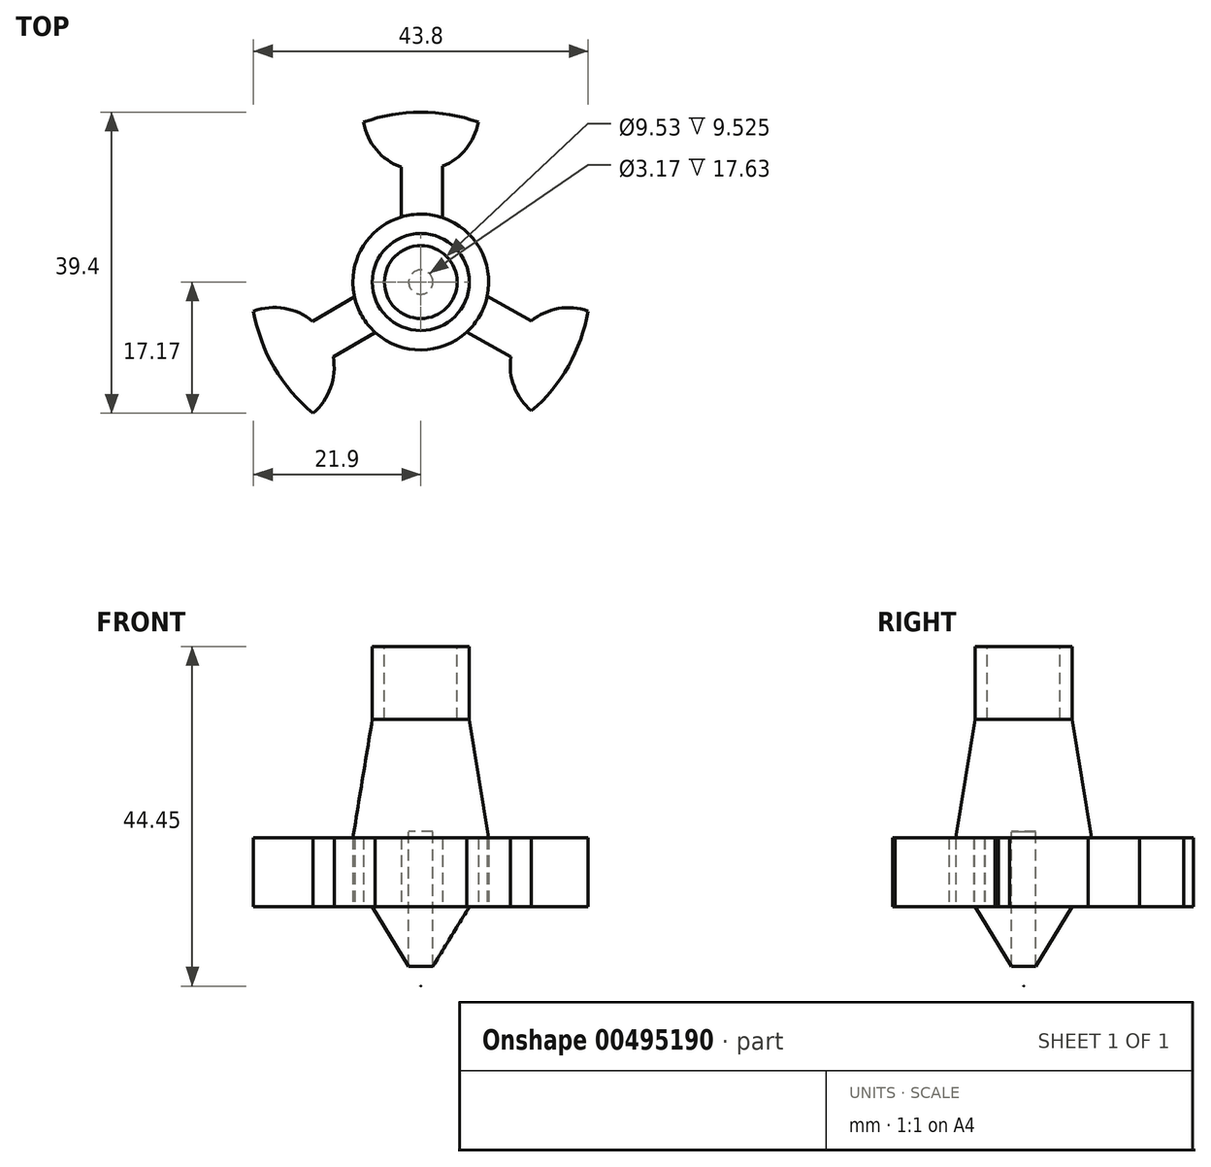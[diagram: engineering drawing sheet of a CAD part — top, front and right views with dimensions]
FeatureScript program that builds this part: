
annotation { "Feature Type Name" : "Feature", "Feature Type Description" : "" }
export const myFeature = defineFeature(function(context is Context, id is Id, definition is map)
    precondition{}
    {
        {
            var Q0;
            Q0=qCreatedBy(makeId("Front.planeOp"),FACE);
            var sketch = newSketch(context, id + "F0", { "sketchPlane" : qUnion([Q0])});
            skLineSegment(sketch, "E0", {"start": v(6.35, 34.05) * mm, "end": v(6.35, 24.53) * mm});
            skLineSegment(sketch, "E1", {"start": v(6.35, 0) * mm, "end": v(0, -10.4) * mm});
            skLineSegment(sketch, "E2.MirrorCS", {"start": v(-6.35, 0) * mm, "end": v(0, -10.4) * mm});
            skLineSegment(sketch, "E3.MirrorCS", {"start": v(-6.35, 34.05) * mm, "end": v(-6.35, 24.53) * mm});
            skLineSegment(sketch, "E4", {"start": v(6.35, 0) * mm, "end": v(22.23, 0) * mm});
            skLineSegment(sketch, "E5", {"start": v(22.23, 0) * mm, "end": v(22.23, 9.01) * mm});
            skLineSegment(sketch, "E6", {"start": v(22.23, 9.01) * mm, "end": v(8.89, 9.01) * mm});
            skLineSegment(sketch, "E7.MirrorCS", {"start": v(-22.23, 9.01) * mm, "end": v(-8.9, 9.01) * mm});
            skLineSegment(sketch, "E8.MirrorCS", {"start": v(-22.23, 0) * mm, "end": v(-22.23, 9.01) * mm});
            skLineSegment(sketch, "E9.MirrorCS", {"start": v(-6.35, 0) * mm, "end": v(-22.23, 0) * mm});
            skLineSegment(sketch, "E10", {"start": v(6.35, 24.53) * mm, "end": v(8.89, 9.01) * mm});
            skLineSegment(sketch, "E11", {"start": v(-6.35, 24.53) * mm, "end": v(-8.9, 9.01) * mm});
            skLineSegment(sketch, "E12", {"start": v(-6.35, 34.05) * mm, "end": v(6.35, 34.05) * mm});
            skLineSegment(sketch, "E13", {"start": v(0, -10.4) * mm, "end": v(0, 34.05) * mm});
            skSolve(sketch);
        }
        {
            var Q0;
            {var subQ0=sQuery(id+"F0.wireOp",EDGE,"E0");Q0=makeQuery(id+"F0.imprint","IMPRINT",FACE,{"disambiguationData":[TD([[makeQuery(id+"F0.imprint","IMPRINT",EDGE,{"derivedFrom":subQ0}),-1.0]])]});}
            var Q1;
            Q1=sQuery(id+"F0.wireOp",EDGE,"E13");
            revolve(context, id + "F1", {"entities" : qUnion([Q0]), "axis" : qUnion([Q1]), "revolveType" : RevolveType.FULL});
        }
        {
            var Q0;
            Q0=qCreatedBy(makeId("Top.planeOp"),FACE);
            var sketch = newSketch(context, id + "F2", { "sketchPlane" : qUnion([Q0])});
            skCircle(sketch, "E14", {"center": v(0, 0) * mm, "radius": 22.23 * mm});
            skArc(sketch, "E15", {"start": v(-7.5, 20.92) * mm, "mid": v(-5.82, 17.31) * mm, "end": v(-2.55, 15.05) * mm});
            skCircle(sketch, "E16", {"center": v(0, 0) * mm, "radius": 8.9 * mm});
            skPoint(sketch, "E17.orphan", {"position": v(0.8, -0.05) * mm});
            skArc(sketch, "E18.trimOffspring", {"start": v(2.83, 15.15) * mm, "mid": v(5.92, 17.42) * mm, "end": v(7.5, 20.92) * mm});
            skArc(sketch, "E19", {"start": v(-14.11, -17.17) * mm, "mid": v(-11.8, -13.83) * mm, "end": v(-11.47, -9.8) * mm});
            skArc(sketch, "E20", {"start": v(21.9, -3.8) * mm, "mid": v(18, -3.47) * mm, "end": v(14.46, -5.11) * mm});
            skLineSegment(sketch, "E21", {"start": v(-2.55, 15.05) * mm, "end": v(-2.55, 8.52) * mm});
            skLineSegment(sketch, "E22", {"start": v(2.83, 15.15) * mm, "end": v(2.83, 8.43) * mm});
            skLineSegment(sketch, "E23.trimOffspring", {"start": v(-11.47, -9.8) * mm, "end": v(-5.97, -6.59) * mm});
            skLineSegment(sketch, "E24.trimOffspring", {"start": v(-14.18, -5.14) * mm, "end": v(-8.68, -1.94) * mm});
            skLineSegment(sketch, "E25", {"start": v(11.8, -9.8) * mm, "end": v(6.04, -6.52) * mm});
            skLineSegment(sketch, "E26.MirrorCS", {"start": v(14.46, -5.11) * mm, "end": v(8.7, -1.84) * mm});
            skArc(sketch, "E27.trimOffspring", {"start": v(11.8, -9.8) * mm, "mid": v(12.2, -13.68) * mm, "end": v(14.49, -16.85) * mm});
            skArc(sketch, "E28.trimOffspring", {"start": v(-14.18, -5.14) * mm, "mid": v(-17.86, -3.44) * mm, "end": v(-21.9, -3.8) * mm});
            skSolve(sketch);
        }
        {
            var Q0;
            {var subQ0=sQuery(id+"F2.wireOp",EDGE,"E19");Q0=makeQuery(id+"F2.imprint","IMPRINT",FACE,{"disambiguationData":[TD([[makeQuery(id+"F2.imprint","IMPRINT",EDGE,{"derivedFrom":subQ0}),-1.0]])]});}
            var Q1;
            {var subQ0=sQuery(id+"F2.wireOp",EDGE,"E18.trimOffspring");Q1=makeQuery(id+"F2.imprint","IMPRINT",FACE,{"disambiguationData":[TD([[makeQuery(id+"F2.imprint","IMPRINT",EDGE,{"derivedFrom":subQ0}),-1.0]])]});}
            var Q2;
            {var subQ3=sQuery(id+"F2.wireOp",EDGE,"E15");Q2=makeQuery(id+"F2.imprint","IMPRINT",FACE,{"disambiguationData":[TD([[makeQuery(id+"F2.imprint","IMPRINT",EDGE,{"derivedFrom":subQ3}),-1.0]])]});}
            extrude(context, id + "F3", {"entities" : qUnion([Q0, Q1, Q2]), "operationType" : NewBodyOperationType.REMOVE, "depth" : 14.1 * mm});
        }
        {
            var Q0;
            Q0=makeQuery(id+"F1.opRevolve","SWEPT_FACE",FACE,{"disambiguationData":[OSD([sQuery(id+"F0.wireOp",EDGE,"E12")])]});
            var sketch = newSketch(context, id + "F4", { "sketchPlane" : qUnion([Q0])});
            skCircle(sketch, "E29", {"center": v(0, 0) * mm, "radius": 4.76 * mm});
            skSolve(sketch);
        }
        {
            var Q0;
            Q0=makeQuery(id+"F4.imprint","IMPRINT",FACE,{"disambiguationData":[TD([[makeQuery(id+"F4.imprint","IMPRINT",EDGE,{"derivedFrom":sQuery(id+"F4.wireOp",EDGE,"E29")}),1.0]])]});
            extrude(context, id + "F5", {"entities" : qUnion([Q0]), "operationType" : NewBodyOperationType.REMOVE, "oppositeDirection" : true, "depth" : 9.52 * mm});
        }
        {
            var Q0;
            Q0=qCreatedBy(makeId("Top.planeOp"),FACE);
            var sketch = newSketch(context, id + "F6", { "sketchPlane" : qUnion([Q0])});
            skCircle(sketch, "E30", {"center": v(0, 0) * mm, "radius": 1.59 * mm});
            skSolve(sketch);
        }
        {
            var Q0;
            Q0 = qSketchRegion(id + "F6", true);
            extrude(context, id + "F7", {"entities" : qUnion([Q0]), "operationType" : NewBodyOperationType.REMOVE, "oppositeDirection" : true, "depth" : 10.4 * mm});
        }
        {
            var Q0;
            Q0=qCreatedBy(makeId("Top.planeOp"),FACE);
            var sketch = newSketch(context, id + "F8", { "sketchPlane" : qUnion([Q0])});
            skCircle(sketch, "E31", {"center": v(0, 0) * mm, "radius": 1.59 * mm});
            skSolve(sketch);
        }
        {
            var Q0;
            Q0=makeQuery(id+"F8.imprint","IMPRINT",FACE,{"disambiguationData":[TD([[makeQuery(id+"F8.imprint","IMPRINT",EDGE,{"derivedFrom":sQuery(id+"F8.wireOp",EDGE,"E31")}),1.0]])]});
            extrude(context, id + "F9", {"entities" : qUnion([Q0]), "operationType" : NewBodyOperationType.REMOVE, "depth" : 9.83 * mm});
        }
    });
